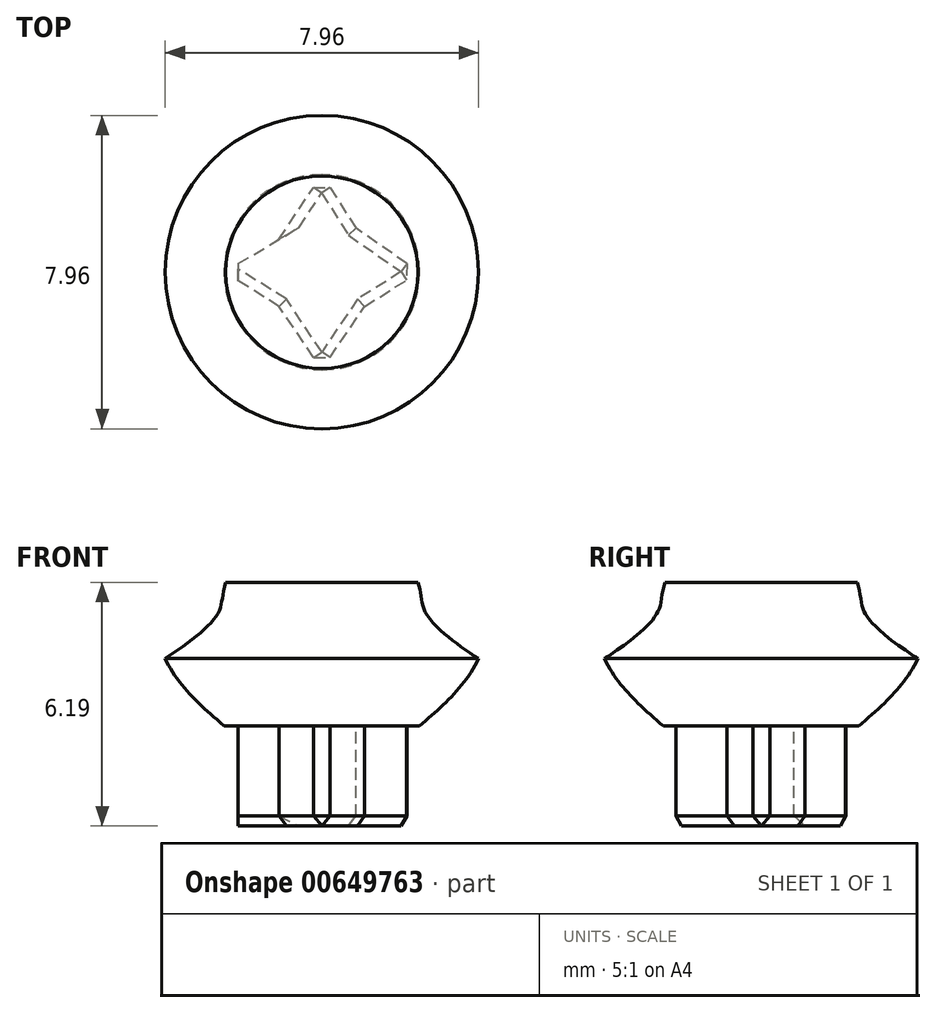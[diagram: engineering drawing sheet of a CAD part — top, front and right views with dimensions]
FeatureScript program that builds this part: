
annotation { "Feature Type Name" : "Feature", "Feature Type Description" : "" }
export const myFeature = defineFeature(function(context is Context, id is Id, definition is map)
    precondition{}
    {
        {
            var Q0;
            Q0=qCreatedBy(makeId("Front.planeOp"),FACE);
            var sketch = newSketch(context, id + "F0", { "sketchPlane" : qUnion([Q0])});
            skFitSpline(sketch, "E0", {"points": [v(2.44, 3.3) * mm, v(2.66, 2.48) * mm, v(3.98, 1.37) * mm], "startDerivative": vector(0.8, -2.82) * mm, "endDerivative": vector(2.58, -1.65) * mm});
            skFitSpline(sketch, "E1", {"points": [v(3.98, 1.37) * mm, v(3.33, 0.45) * mm, v(2.48, -0.34) * mm], "startDerivative": vector(-0.8, -1.94) * mm, "endDerivative": vector(-2.33, -2.04) * mm});
            skLineSegment(sketch, "E2", {"start": v(2.44, 3.3) * mm, "end": v(0, 3.3) * mm});
            skLineSegment(sketch, "E3", {"start": v(2.48, -0.34) * mm, "end": v(0, -0.34) * mm});
            skLineSegment(sketch, "E4", {"start": v(0, -0.34) * mm, "end": v(0, 3.3) * mm});
            skSolve(sketch);
        }
        {
            var Q0;
            Q0=makeQuery(id+"F0.imprint","IMPRINT",FACE,{"disambiguationData":[TD([[makeQuery(id+"F0.imprint","IMPRINT",EDGE,{"derivedFrom":sQuery(id+"F0.wireOp",EDGE,"E0")}),-1.0]])]});
            var Q1;
            Q1=sQuery(id+"F0.wireOp",EDGE,"E4");
            revolve(context, id + "F1", {"entities" : qUnion([Q0]), "axis" : qUnion([Q1]), "revolveType" : RevolveType.FULL});
        }
        {
            var Q0;
            Q0=makeQuery(id+"F1.opRevolve","SWEPT_FACE",FACE,{"disambiguationData":[OSD([sQuery(id+"F0.wireOp",EDGE,"E3")])]});
            var sketch = newSketch(context, id + "F2", { "sketchPlane" : qUnion([Q0])});
            skLineSegment(sketch, "E5", {"start": v(0, 2.48) * mm, "end": v(-1.08, 0.87) * mm});
            skLineSegment(sketch, "E6.MirrorCS", {"start": v(0, 2.48) * mm, "end": v(1.08, 0.87) * mm});
            skLineSegment(sketch, "E7.MirrorCS", {"start": v(1.08, 0.87) * mm, "end": v(0, 0) * mm});
            skLineSegment(sketch, "E8", {"start": v(-1.08, 0.87) * mm, "end": v(-2.48, 0) * mm});
            skLineSegment(sketch, "E9", {"start": v(-2.48, 0) * mm, "end": v(-1.08, -0.84) * mm});
            skLineSegment(sketch, "E10", {"start": v(-1.08, -0.84) * mm, "end": v(0, 0) * mm});
            skLineSegment(sketch, "E11", {"start": v(-1.08, -0.84) * mm, "end": v(0, -2.48) * mm});
            skLineSegment(sketch, "E12", {"start": v(0, -2.48) * mm, "end": v(0.86, -1.12) * mm});
            skLineSegment(sketch, "E13", {"start": v(0.86, -1.12) * mm, "end": v(0, 0) * mm});
            skLineSegment(sketch, "E14", {"start": v(1.08, 0.87) * mm, "end": v(2.48, 0) * mm});
            skLineSegment(sketch, "E15", {"start": v(2.48, 0) * mm, "end": v(0.86, -1.12) * mm});
            skLineSegment(sketch, "E16", {"start": v(0, 0) * mm, "end": v(-1.08, 0.87) * mm});
            skSolve(sketch);
        }
        {
            var Q0;
            Q0=makeQuery(id+"F2.imprint","IMPRINT",FACE,{"disambiguationData":[TD([[makeQuery(id+"F2.imprint","IMPRINT",EDGE,{"derivedFrom":sQuery(id+"F2.wireOp",EDGE,"E5")}),1.0]])]});
            var Q1;
            Q1=makeQuery(id+"F2.imprint","IMPRINT",FACE,{"disambiguationData":[TD([[makeQuery(id+"F2.imprint","IMPRINT",EDGE,{"derivedFrom":sQuery(id+"F2.wireOp",EDGE,"ocl75Qjl-pxYA-1WOj-SxRw-egUaijb2k4DK")}),-1.0]])]});
            var Q2;
            Q2=makeQuery(id+"F2.imprint","IMPRINT",FACE,{"disambiguationData":[TD([[makeQuery(id+"F2.imprint","IMPRINT",EDGE,{"derivedFrom":sQuery(id+"F2.wireOp",EDGE,"E10")}),-1.0]])]});
            var Q3;
            Q3=makeQuery(id+"F2.imprint","IMPRINT",FACE,{"disambiguationData":[TD([[makeQuery(id+"F2.imprint","IMPRINT",EDGE,{"derivedFrom":sQuery(id+"F2.wireOp",EDGE,"E7.MirrorCS")}),1.0]])]});
            var Q4;
            Q4=makeQuery(id+"F2.imprint","IMPRINT",FACE,{"disambiguationData":[TD([[makeQuery(id+"F2.imprint","IMPRINT",EDGE,{"derivedFrom":sQuery(id+"F2.wireOp",EDGE,"E8")}),1.0]])]});
            extrude(context, id + "F3", {"entities" : qUnion([Q0, Q1, Q2, Q3, Q4]), "operationType" : NewBodyOperationType.ADD, "depth" : 2.54 * mm, "offsetDistance" : 25.4 * mm});
        }
        {
            var Q0;
            Q0=makeQuery(id+"F3.opExtrude","CAP_EDGE",EDGE,{"disambiguationData":[OSD([sQuery(id+"F2.wireOp",EDGE,"E6.MirrorCS")])],"isStart":false});
            var Q1;
            Q1=makeQuery(id+"F3.opExtrude","CAP_EDGE",EDGE,{"disambiguationData":[OSD([sQuery(id+"F2.wireOp",EDGE,"E14")])],"isStart":false});
            var Q2;
            Q2=makeQuery(id+"F3.opExtrude","CAP_EDGE",EDGE,{"disambiguationData":[OSD([sQuery(id+"F2.wireOp",EDGE,"E15")])],"isStart":false});
            var Q3;
            Q3=makeQuery(id+"F3.opExtrude","CAP_EDGE",EDGE,{"disambiguationData":[OSD([sQuery(id+"F2.wireOp",EDGE,"E12")])],"isStart":false});
            var Q4;
            Q4=makeQuery(id+"F3.opExtrude","CAP_EDGE",EDGE,{"disambiguationData":[OSD([sQuery(id+"F2.wireOp",EDGE,"E11")])],"isStart":false});
            var Q5;
            Q5=makeQuery(id+"F3.opExtrude","CAP_EDGE",EDGE,{"disambiguationData":[OSD([sQuery(id+"F2.wireOp",EDGE,"E8")])],"isStart":false});
            var Q6;
            Q6=makeQuery(id+"F3.opExtrude","CAP_EDGE",EDGE,{"disambiguationData":[OSD([sQuery(id+"F2.wireOp",EDGE,"E5")])],"isStart":false});
            var Q7;
            Q7=makeQuery(id+"F3.opExtrude","SWEPT_EDGE",EDGE,{"disambiguationData":[OSD([sQuery(id+"F0.wireOp",EDGE,"E1"),sQuery(id+"F0.wireOp",EDGE,"E3"),sQuery(id+"F2.wireOp",EDGE,"E5"),sQuery(id+"F2.wireOp",EDGE,"E6.MirrorCS")])]});
            var Q8;
            Q8=makeQuery(id+"F3.opExtrude","SWEPT_EDGE",EDGE,{"disambiguationData":[OSD([sQuery(id+"F0.wireOp",EDGE,"E1"),sQuery(id+"F0.wireOp",EDGE,"E3"),sQuery(id+"F2.wireOp",EDGE,"E14"),sQuery(id+"F2.wireOp",EDGE,"E15")])]});
            var Q9;
            Q9=makeQuery(id+"F3.opExtrude","SWEPT_EDGE",EDGE,{"disambiguationData":[OSD([sQuery(id+"F0.wireOp",EDGE,"E1"),sQuery(id+"F0.wireOp",EDGE,"E3"),sQuery(id+"F2.wireOp",EDGE,"E11"),sQuery(id+"F2.wireOp",EDGE,"E12")])]});
            var Q10;
            Q10=makeQuery(id+"F3.opExtrude","SWEPT_EDGE",EDGE,{"disambiguationData":[OSD([sQuery(id+"F0.wireOp",EDGE,"E1"),sQuery(id+"F0.wireOp",EDGE,"E3"),sQuery(id+"F2.wireOp",EDGE,"E8"),sQuery(id+"F2.wireOp",EDGE,"E9")])]});
            chamfer(context, id + "F4", {"entities" : qUnion([Q0, Q1, Q2, Q3, Q4, Q5, Q6, Q7, Q8, Q9, Q10]), "width" : 0.25 * mm, "tangentPropagation" : true});
        }
    });
